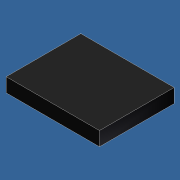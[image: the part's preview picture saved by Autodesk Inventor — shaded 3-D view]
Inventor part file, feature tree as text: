
AUTODESK INVENTOR PART (.ipt)
format: ipt  version: unknown  size: 165,888 bytes
history: native  units: mm
features: extrude x1, sketch x1
ambient origin geometry x8: Origin, YZ Plane, XZ Plane, XY Plane, X Axis, Y Axis, Z Axis, Center Point
feature tree (2):
  extrude  "Выдавливание2"  Depth=10.0mm
  sketch  "Эскиз2"
